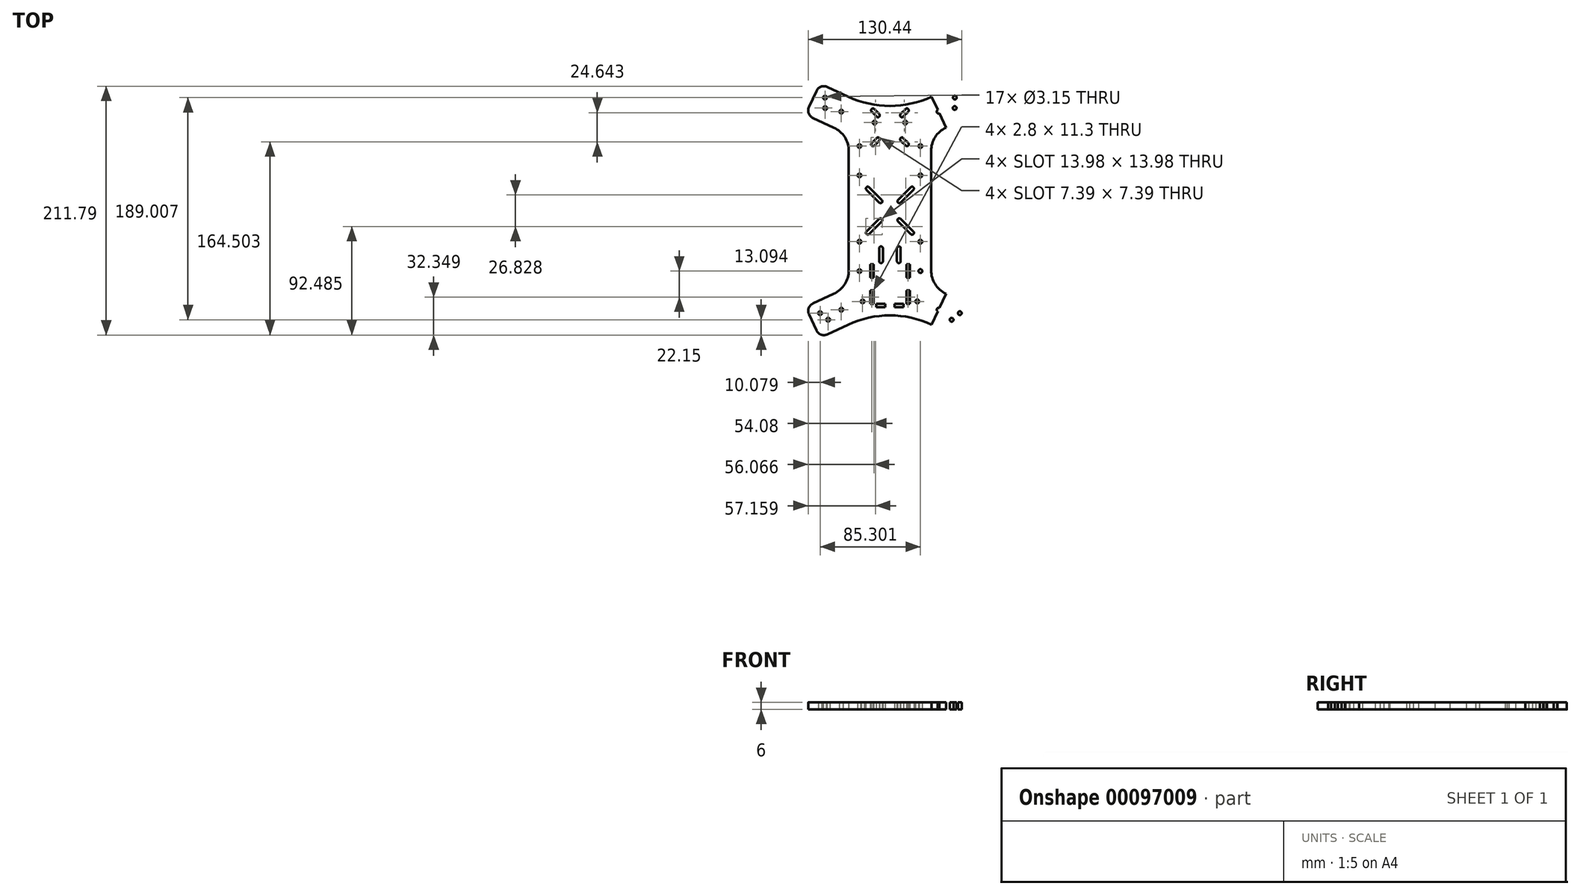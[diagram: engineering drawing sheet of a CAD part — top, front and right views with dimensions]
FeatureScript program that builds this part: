
annotation { "Feature Type Name" : "Feature", "Feature Type Description" : "" }
export const myFeature = defineFeature(function(context is Context, id is Id, definition is map)
    precondition{}
    {
        {
            var Q0;
            Q0=qCreatedBy(makeId("Top.planeOp"),FACE);
            var sketch = newSketch(context, id + "F0", { "sketchPlane" : qUnion([Q0])});
            skPoint(sketch, "E0", {"position": v(0, -1.46) * mm});
            skLineSegment(sketch, "E1", {"start": v(-16.8, -69.36) * mm, "end": v(-14, -69.36) * mm});
            skLineSegment(sketch, "E2", {"start": v(-16.8, -58.51) * mm, "end": v(-14, -58.51) * mm});
            skLineSegment(sketch, "E3", {"start": v(16.8, -47.21) * mm, "end": v(16.8, -58.51) * mm});
            skLineSegment(sketch, "E4", {"start": v(-16.8, -47.21) * mm, "end": v(-16.8, -58.51) * mm});
            skLineSegment(sketch, "E5.trimOffspring", {"start": v(-16.8, -47.21) * mm, "end": v(-14, -47.21) * mm});
            skLineSegment(sketch, "E6", {"start": v(-11.5, -80.66) * mm, "end": v(-11.5, -83.46) * mm});
            skLineSegment(sketch, "E7", {"start": v(11.5, -80.66) * mm, "end": v(11.5, -83.46) * mm});
            skLineSegment(sketch, "E8", {"start": v(4, -80.66) * mm, "end": v(4, -83.46) * mm});
            skLineSegment(sketch, "E9", {"start": v(-4, -80.66) * mm, "end": v(-4, -83.46) * mm});
            skLineSegment(sketch, "E10.trimOffspring", {"start": v(14, -69.36) * mm, "end": v(14, -80.66) * mm});
            skLineSegment(sketch, "E11.trimOffspring", {"start": v(-14, -69.36) * mm, "end": v(-14, -80.66) * mm});
            skLineSegment(sketch, "E12.trimOffspring", {"start": v(14, -69.36) * mm, "end": v(16.8, -69.36) * mm});
            skLineSegment(sketch, "E13.trimOffspring", {"start": v(14, -58.51) * mm, "end": v(16.8, -58.51) * mm});
            skLineSegment(sketch, "E14.trimOffspring", {"start": v(14, -47.21) * mm, "end": v(16.8, -47.21) * mm});
            skLineSegment(sketch, "E15.trimOffspring", {"start": v(14, -47.21) * mm, "end": v(14, -58.51) * mm});
            skLineSegment(sketch, "E16.trimOffspring", {"start": v(-14, -47.21) * mm, "end": v(-14, -58.51) * mm});
            skLineSegment(sketch, "E17", {"start": v(-16.8, -69.36) * mm, "end": v(-16.8, -80.66) * mm});
            skLineSegment(sketch, "E18", {"start": v(16.8, -69.36) * mm, "end": v(16.8, -80.66) * mm});
            skCircle(sketch, "E19", {"center": v(23.23, -78.7) * mm, "radius": 1.57 * mm});
            skCircle(sketch, "E20", {"center": v(-23.23, -78.7) * mm, "radius": 1.57 * mm});
            skCircle(sketch, "E21", {"center": v(-25.9, -52.86) * mm, "radius": 1.57 * mm});
            skCircle(sketch, "E22", {"center": v(25.9, -52.86) * mm, "radius": 1.57 * mm});
            skCircle(sketch, "E23", {"center": v(-13.04, 73.48) * mm, "radius": 1.57 * mm});
            skCircle(sketch, "E24", {"center": v(13.04, 73.48) * mm, "radius": 1.57 * mm});
            skCircle(sketch, "E25", {"center": v(-25.9, 53.54) * mm, "radius": 1.57 * mm});
            skCircle(sketch, "E26", {"center": v(25.9, 53.54) * mm, "radius": 1.57 * mm});
            skLineSegment(sketch, "E27", {"start": v(-16.8, -80.66) * mm, "end": v(-14, -80.66) * mm});
            skLineSegment(sketch, "E28", {"start": v(-11.5, -83.46) * mm, "end": v(-4, -83.46) * mm});
            skLineSegment(sketch, "E29.trimOffspring", {"start": v(4, -80.66) * mm, "end": v(11.5, -80.66) * mm});
            skLineSegment(sketch, "E30.trimOffspring", {"start": v(4, -83.46) * mm, "end": v(11.5, -83.46) * mm});
            skLineSegment(sketch, "E31.trimOffspring", {"start": v(-11.5, -80.66) * mm, "end": v(-4, -80.66) * mm});
            skLineSegment(sketch, "E32.trimOffspring", {"start": v(14, -80.66) * mm, "end": v(16.8, -80.66) * mm});
            skCircle(sketch, "E33", {"center": v(-59.4, -88.64) * mm, "radius": 1.57 * mm});
            skCircle(sketch, "E34", {"center": v(-52.49, -94.27) * mm, "radius": 1.57 * mm});
            skCircle(sketch, "E35", {"center": v(-41.34, -85.73) * mm, "radius": 1.57 * mm});
            skLineSegment(sketch, "E36", {"start": v(-57.3, -93.14) * mm, "end": v(-41.36, -85.7) * mm});
            skCircle(sketch, "E37", {"center": v(-55.2, 94.74) * mm, "radius": 1.57 * mm});
            skCircle(sketch, "E38", {"center": v(-55.06, 85.83) * mm, "radius": 1.57 * mm});
            skCircle(sketch, "E39", {"center": v(-41.34, 82.8) * mm, "radius": 1.57 * mm});
            skLineSegment(sketch, "E40", {"start": v(-57.3, 90.25) * mm, "end": v(-41.34, 82.8) * mm});
            skLineSegment(sketch, "E41.MirrorCS", {"start": v(57.29, 90.26) * mm, "end": v(41.34, 82.82) * mm});
            skCircle(sketch, "E42.MirrorC", {"center": v(55.19, 94.75) * mm, "radius": 1.57 * mm});
            skCircle(sketch, "E43.MirrorC", {"center": v(55.05, 85.84) * mm, "radius": 1.57 * mm});
            skCircle(sketch, "E44.MirrorC", {"center": v(41.34, 82.8) * mm, "radius": 1.57 * mm});
            skLineSegment(sketch, "E45.MirrorCS", {"start": v(57.3, -93.17) * mm, "end": v(41.34, -85.73) * mm});
            skCircle(sketch, "E46.MirrorC", {"center": v(59.39, -88.67) * mm, "radius": 1.57 * mm});
            skCircle(sketch, "E47.MirrorC", {"center": v(52.47, -94.3) * mm, "radius": 1.57 * mm});
            skCircle(sketch, "E48.MirrorC", {"center": v(41.34, -85.73) * mm, "radius": 1.57 * mm});
            skLineSegment(sketch, "E49", {"start": v(55.05, 85.84) * mm, "end": v(53.76, 88.61) * mm});
            skLineSegment(sketch, "E50", {"start": v(55.19, 94.75) * mm, "end": v(57.29, 90.26) * mm});
            skLineSegment(sketch, "E51", {"start": v(57.29, 90.26) * mm, "end": v(65.44, 94.06) * mm});
            skLineSegment(sketch, "E52", {"start": v(-55.06, 85.83) * mm, "end": v(-53.77, 88.6) * mm});
            skLineSegment(sketch, "E53", {"start": v(-55.2, 94.74) * mm, "end": v(-57.3, 90.25) * mm});
            skLineSegment(sketch, "E54", {"start": v(-57.3, 90.25) * mm, "end": v(-65.45, 94.05) * mm});
            skLineSegment(sketch, "E55", {"start": v(-52.49, -94.27) * mm, "end": v(-53.78, -91.5) * mm});
            skLineSegment(sketch, "E56", {"start": v(-59.4, -88.64) * mm, "end": v(-57.3, -93.14) * mm});
            skLineSegment(sketch, "E57", {"start": v(52.47, -94.3) * mm, "end": v(53.77, -91.52) * mm});
            skLineSegment(sketch, "E58", {"start": v(59.39, -88.67) * mm, "end": v(57.3, -93.17) * mm});
            skLineSegment(sketch, "E59", {"start": v(57.3, -93.17) * mm, "end": v(65.45, -96.97) * mm});
            skLineSegment(sketch, "E60", {"start": v(-57.3, -93.14) * mm, "end": v(-65.46, -96.94) * mm});
            skLineSegment(sketch, "E61", {"start": v(-65.45, 94.05) * mm, "end": v(-62.49, 100.4) * mm});
            skLineSegment(sketch, "E62", {"start": v(-65.45, 94.05) * mm, "end": v(-68.83, 86.8) * mm});
            skLineSegment(sketch, "E63", {"start": v(65.44, 94.06) * mm, "end": v(68.79, 86.89) * mm});
            skLineSegment(sketch, "E64", {"start": v(65.44, 94.06) * mm, "end": v(62.49, 100.4) * mm});
            skLineSegment(sketch, "E65", {"start": v(65.45, -96.97) * mm, "end": v(68.83, -89.72) * mm});
            skLineSegment(sketch, "E66", {"start": v(65.45, -96.97) * mm, "end": v(62.49, -103.31) * mm});
            skLineSegment(sketch, "E67", {"start": v(-65.46, -96.94) * mm, "end": v(-68.83, -89.72) * mm});
            skLineSegment(sketch, "E68", {"start": v(-65.46, -96.94) * mm, "end": v(-62.5, -103.3) * mm});
            skLineSegment(sketch, "E69", {"start": v(-13.04, 73.48) * mm, "end": v(-13.04, 71.9) * mm});
            skLineSegment(sketch, "E70", {"start": v(13.04, 73.48) * mm, "end": v(13.04, 71.9) * mm});
            skLineSegment(sketch, "E71", {"start": v(13.04, 71.9) * mm, "end": v(-13.04, 71.9) * mm});
            skLineSegment(sketch, "E72", {"start": v(-4, -83.46) * mm, "end": v(4, -83.46) * mm});
            skLineSegment(sketch, "E73", {"start": v(0, -1.46) * mm, "end": v(0, 14.54) * mm});
            skLineSegment(sketch, "E74", {"start": v(0, -1.46) * mm, "end": v(0, -17.46) * mm});
            skLineSegment(sketch, "E75", {"start": v(-25.9, 53.54) * mm, "end": v(-25.9, 51.96) * mm});
            skLineSegment(sketch, "E76", {"start": v(25.9, 51.96) * mm, "end": v(25.9, 53.54) * mm});
            skLineSegment(sketch, "E77", {"start": v(0, -1.46) * mm, "end": v(-16, -1.46) * mm});
            skLineSegment(sketch, "E78", {"start": v(0, -1.46) * mm, "end": v(16, -1.46) * mm});
            skLineSegment(sketch, "E79", {"start": v(-41.34, -85.73) * mm, "end": v(-35.43, -98.42) * mm});
            skLineSegment(sketch, "E80", {"start": v(-41.34, -85.73) * mm, "end": v(-47.68, -72.14) * mm});
            skLineSegment(sketch, "E81", {"start": v(-35.43, -98.42) * mm, "end": v(-53.19, -106.7) * mm});
            skLineSegment(sketch, "E82", {"start": v(-47.68, -72.14) * mm, "end": v(-65.44, -80.42) * mm});
            skLineSegment(sketch, "E83", {"start": v(41.34, -85.73) * mm, "end": v(35.43, -98.42) * mm});
            skLineSegment(sketch, "E84", {"start": v(41.34, -85.73) * mm, "end": v(47.68, -72.14) * mm});
            skLineSegment(sketch, "E85", {"start": v(47.68, -72.14) * mm, "end": v(65.44, -80.42) * mm});
            skLineSegment(sketch, "E86", {"start": v(35.43, -98.42) * mm, "end": v(53.19, -106.7) * mm});
            skLineSegment(sketch, "E87", {"start": v(-41.34, 82.8) * mm, "end": v(-35.43, 95.5) * mm});
            skLineSegment(sketch, "E88", {"start": v(-41.34, 82.8) * mm, "end": v(-47.68, 69.21) * mm});
            skLineSegment(sketch, "E89", {"start": v(41.34, 82.8) * mm, "end": v(35.43, 95.5) * mm});
            skLineSegment(sketch, "E90", {"start": v(41.34, 82.8) * mm, "end": v(47.68, 69.21) * mm});
            skLineSegment(sketch, "E91", {"start": v(35.43, 95.5) * mm, "end": v(53.19, 103.78) * mm});
            skLineSegment(sketch, "E92", {"start": v(47.68, 69.21) * mm, "end": v(65.44, 77.5) * mm});
            skLineSegment(sketch, "E93", {"start": v(-35.43, 95.5) * mm, "end": v(-53.19, 103.78) * mm});
            skLineSegment(sketch, "E94", {"start": v(-47.68, 69.21) * mm, "end": v(-65.44, 77.5) * mm});
            skLineSegment(sketch, "E95", {"start": v(-41.34, -85.73) * mm, "end": v(-35, -82.77) * mm});
            skLineSegment(sketch, "E96", {"start": v(41.34, -85.73) * mm, "end": v(35, -82.77) * mm});
            skLineSegment(sketch, "E97", {"start": v(-41.34, 82.8) * mm, "end": v(-35, 79.85) * mm});
            skLineSegment(sketch, "E98", {"start": v(41.34, 82.8) * mm, "end": v(35, 79.85) * mm});
            skLineSegment(sketch, "E99", {"start": v(16, -1.46) * mm, "end": v(35, -1.46) * mm});
            skLineSegment(sketch, "E100", {"start": v(-16, -1.46) * mm, "end": v(-35, -1.46) * mm});
            skLineSegment(sketch, "E101", {"start": v(35, -1.46) * mm, "end": v(35, 38.54) * mm});
            skLineSegment(sketch, "E102", {"start": v(35, -1.46) * mm, "end": v(35, -41.46) * mm});
            skLineSegment(sketch, "E103", {"start": v(-35, -1.46) * mm, "end": v(-35, 38.54) * mm});
            skLineSegment(sketch, "E104", {"start": v(-35, -1.46) * mm, "end": v(-35, -41.46) * mm});
            skLineSegment(sketch, "E105", {"start": v(-35, -41.46) * mm, "end": v(35, -41.46) * mm});
            skLineSegment(sketch, "E106", {"start": v(-35, 38.54) * mm, "end": v(35, 38.54) * mm});
            skLineSegment(sketch, "E107", {"start": v(-25.9, -52.86) * mm, "end": v(-25.9, -54.44) * mm});
            skLineSegment(sketch, "E108", {"start": v(-25.9, -54.44) * mm, "end": v(25.9, -54.44) * mm});
            skLineSegment(sketch, "E109", {"start": v(25.9, -54.44) * mm, "end": v(25.9, -52.86) * mm});
            skLineSegment(sketch, "E110", {"start": v(-23.23, -78.7) * mm, "end": v(-23.23, -80.27) * mm});
            skLineSegment(sketch, "E111", {"start": v(-23.23, -80.27) * mm, "end": v(23.23, -80.27) * mm});
            skLineSegment(sketch, "E112", {"start": v(23.23, -80.27) * mm, "end": v(23.23, -78.7) * mm});
            skLineSegment(sketch, "E113", {"start": v(35, 79.85) * mm, "end": v(35, 38.54) * mm});
            skLineSegment(sketch, "E114", {"start": v(35, -41.46) * mm, "end": v(35, -82.77) * mm});
            skLineSegment(sketch, "E115", {"start": v(-35, -82.77) * mm, "end": v(-35, -41.46) * mm});
            skLineSegment(sketch, "E116", {"start": v(-35, 38.54) * mm, "end": v(-35, 79.85) * mm});
            skLineSegment(sketch, "E117", {"start": v(-13.77, 14.54) * mm, "end": v(0, 14.54) * mm});
            skLineSegment(sketch, "E118", {"start": v(0, 14.54) * mm, "end": v(13.77, 14.54) * mm});
            skLineSegment(sketch, "E119", {"start": v(16, 12.31) * mm, "end": v(16, -1.46) * mm});
            skLineSegment(sketch, "E120", {"start": v(16, -1.46) * mm, "end": v(16, -15.23) * mm});
            skLineSegment(sketch, "E121", {"start": v(13.77, -17.46) * mm, "end": v(0, -17.46) * mm});
            skLineSegment(sketch, "E122", {"start": v(0, -17.46) * mm, "end": v(-13.77, -17.46) * mm});
            skLineSegment(sketch, "E123", {"start": v(-16, -15.23) * mm, "end": v(-16, -1.46) * mm});
            skLineSegment(sketch, "E124", {"start": v(-16, -1.46) * mm, "end": v(-16, 12.31) * mm});
            skPoint(sketch, "E125", {"position": v(-35, 49.3) * mm});
            skPoint(sketch, "E126", {"position": v(35, 49.3) * mm});
            skPoint(sketch, "E127", {"position": v(-35, -52.23) * mm});
            skPoint(sketch, "E128", {"position": v(35, -52.23) * mm});
            skLineSegment(sketch, "E129", {"start": v(0, -54.44) * mm, "end": v(0, -80.27) * mm});
            skLineSegment(sketch, "E130", {"start": v(0, -80.27) * mm, "end": v(0, -83.46) * mm});
            skLineSegment(sketch, "E131", {"start": v(47.68, 69.21) * mm, "end": v(35, 63.3) * mm});
            skLineSegment(sketch, "E132", {"start": v(-47.68, 69.21) * mm, "end": v(-35, 63.3) * mm});
            skLineSegment(sketch, "E133", {"start": v(47.68, -72.14) * mm, "end": v(35, -66.22) * mm});
            skLineSegment(sketch, "E134", {"start": v(-47.68, -72.14) * mm, "end": v(-35, -66.22) * mm});
            skArc(sketch, "E135", {"start": v(-47.68, 69.21) * mm, "mid": v(-38.44, 61.1) * mm, "end": v(-35, 49.3) * mm});
            skArc(sketch, "E136", {"start": v(47.68, 69.21) * mm, "mid": v(38.44, 61.1) * mm, "end": v(35, 49.3) * mm});
            skArc(sketch, "E137", {"start": v(47.68, -72.14) * mm, "mid": v(38.44, -64.03) * mm, "end": v(35, -52.23) * mm});
            skArc(sketch, "E138", {"start": v(-47.68, -72.14) * mm, "mid": v(-38.44, -64.03) * mm, "end": v(-35, -52.23) * mm});
            skArc(sketch, "E139", {"start": v(35.43, 95.5) * mm, "mid": v(0, 87.64) * mm, "end": v(-35.43, 95.5) * mm});
            skArc(sketch, "E140", {"start": v(35.43, -98.42) * mm, "mid": v(0, -90.57) * mm, "end": v(-35.43, -98.42) * mm});
            skLineSegment(sketch, "E141", {"start": v(0, -83.46) * mm, "end": v(0, -90.57) * mm});
            skLineSegment(sketch, "E142", {"start": v(0, 71.9) * mm, "end": v(0, 87.64) * mm});
            skLineSegment(sketch, "E143", {"start": v(0, 71.9) * mm, "end": v(0, 51.96) * mm});
            skLineSegment(sketch, "E144", {"start": v(-25.9, 51.96) * mm, "end": v(25.9, 51.96) * mm});
            skLineSegment(sketch, "E145", {"start": v(-25.9, -52.86) * mm, "end": v(-25.9, 53.54) * mm});
            skLineSegment(sketch, "E146", {"start": v(25.9, 53.54) * mm, "end": v(25.9, -52.86) * mm});
            skPoint(sketch, "E147", {"position": v(25.9, -27.86) * mm});
            skPoint(sketch, "E148", {"position": v(-25.9, -27.86) * mm});
            skPoint(sketch, "E149", {"position": v(-25.9, 28.54) * mm});
            skPoint(sketch, "E150", {"position": v(25.9, 28.54) * mm});
            skCircle(sketch, "E151", {"center": v(25.9, 28.54) * mm, "radius": 1.57 * mm});
            skCircle(sketch, "E152", {"center": v(-25.9, 28.54) * mm, "radius": 1.57 * mm});
            skCircle(sketch, "E153", {"center": v(-25.9, -27.86) * mm, "radius": 1.57 * mm});
            skCircle(sketch, "E154", {"center": v(25.9, -27.86) * mm, "radius": 1.57 * mm});
            skPoint(sketch, "E155", {"position": v(0, -41.46) * mm});
            skPoint(sketch, "E156", {"position": v(-6, -41.46) * mm});
            skPoint(sketch, "E157", {"position": v(6, -41.46) * mm});
            skPoint(sketch, "E158", {"position": v(9.15, -41.46) * mm});
            skPoint(sketch, "E159", {"position": v(-9.15, -41.46) * mm});
            skLineSegment(sketch, "E160", {"start": v(-9.15, -41.46) * mm, "end": v(-9.15, -33.46) * mm});
            skLineSegment(sketch, "E161", {"start": v(-6, -41.46) * mm, "end": v(-6, -33.46) * mm});
            skLineSegment(sketch, "E162", {"start": v(6, -41.46) * mm, "end": v(6, -33.46) * mm});
            skLineSegment(sketch, "E163", {"start": v(9.15, -41.46) * mm, "end": v(9.15, -33.46) * mm});
            skLineSegment(sketch, "E164", {"start": v(-9.15, -41.46) * mm, "end": v(-9.15, -44.46) * mm});
            skLineSegment(sketch, "E165", {"start": v(-6, -41.46) * mm, "end": v(-6, -44.46) * mm});
            skLineSegment(sketch, "E166", {"start": v(6, -41.46) * mm, "end": v(6, -44.46) * mm});
            skLineSegment(sketch, "E167", {"start": v(9.15, -41.46) * mm, "end": v(9.15, -44.46) * mm});
            skArc(sketch, "E168", {"start": v(-6, -33.46) * mm, "mid": v(-7.58, -31.89) * mm, "end": v(-9.15, -33.46) * mm});
            skArc(sketch, "E169", {"start": v(-9.15, -44.46) * mm, "mid": v(-7.58, -46.04) * mm, "end": v(-6, -44.46) * mm});
            skArc(sketch, "E170", {"start": v(6, -44.46) * mm, "mid": v(7.57, -46.04) * mm, "end": v(9.15, -44.46) * mm});
            skArc(sketch, "E171", {"start": v(9.15, -33.46) * mm, "mid": v(7.57, -31.89) * mm, "end": v(6, -33.46) * mm});
            skLineSegment(sketch, "E172", {"start": v(0, -1.46) * mm, "end": v(6.89, 5.43) * mm});
            skLineSegment(sketch, "E173", {"start": v(0, -1.46) * mm, "end": v(-6.89, 5.43) * mm});
            skLineSegment(sketch, "E174", {"start": v(0, -1.46) * mm, "end": v(6.89, -8.35) * mm});
            skLineSegment(sketch, "E175", {"start": v(0, -1.46) * mm, "end": v(-6.89, -8.35) * mm});
            skArc(sketch, "E176", {"start": v(17.71, -21.4) * mm, "mid": v(19.94, -21.4) * mm, "end": v(19.94, -19.18) * mm});
            skArc(sketch, "E177", {"start": v(-19.94, -19.18) * mm, "mid": v(-19.94, -21.4) * mm, "end": v(-17.71, -21.4) * mm});
            skArc(sketch, "E178", {"start": v(-17.71, 18.48) * mm, "mid": v(-19.94, 18.48) * mm, "end": v(-19.94, 16.25) * mm});
            skArc(sketch, "E179", {"start": v(19.94, 16.25) * mm, "mid": v(19.94, 18.48) * mm, "end": v(17.71, 18.48) * mm});
            skPoint(sketch, "E180", {"position": v(8, 6.54) * mm});
            skPoint(sketch, "E181", {"position": v(-8, 6.54) * mm});
            skPoint(sketch, "E182", {"position": v(8, -9.46) * mm});
            skPoint(sketch, "E183", {"position": v(-8, -9.46) * mm});
            skArc(sketch, "E184", {"start": v(6.89, 7.65) * mm, "mid": v(6.89, 5.43) * mm, "end": v(9.11, 5.43) * mm});
            skArc(sketch, "E185", {"start": v(-9.11, 5.43) * mm, "mid": v(-6.89, 5.43) * mm, "end": v(-6.89, 7.65) * mm});
            skArc(sketch, "E186", {"start": v(9.11, -8.35) * mm, "mid": v(6.89, -8.35) * mm, "end": v(6.89, -10.57) * mm});
            skArc(sketch, "E187", {"start": v(-6.89, -10.57) * mm, "mid": v(-6.89, -8.35) * mm, "end": v(-9.11, -8.35) * mm});
            skLineSegment(sketch, "E188", {"start": v(17.71, 18.48) * mm, "end": v(6.89, 7.65) * mm});
            skLineSegment(sketch, "E189", {"start": v(9.11, 5.43) * mm, "end": v(19.94, 16.25) * mm});
            skLineSegment(sketch, "E190", {"start": v(-6.89, 7.65) * mm, "end": v(-17.71, 18.48) * mm});
            skLineSegment(sketch, "E191", {"start": v(-19.94, 16.25) * mm, "end": v(-9.11, 5.43) * mm});
            skLineSegment(sketch, "E192", {"start": v(17.71, -21.4) * mm, "end": v(6.89, -10.57) * mm});
            skLineSegment(sketch, "E193", {"start": v(9.11, -8.35) * mm, "end": v(19.94, -19.18) * mm});
            skLineSegment(sketch, "E194", {"start": v(-6.89, -10.57) * mm, "end": v(-17.71, -21.4) * mm});
            skLineSegment(sketch, "E195", {"start": v(-19.94, -19.18) * mm, "end": v(-9.11, -8.35) * mm});
            skPoint(sketch, "E196", {"position": v(-19.94, -21.4) * mm});
            skPoint(sketch, "E197", {"position": v(62.49, -103.31) * mm});
            skPoint(sketch, "E198", {"position": v(68.83, -89.72) * mm});
            skPoint(sketch, "E199", {"position": v(65.44, -80.42) * mm});
            skPoint(sketch, "E200", {"position": v(53.19, -106.7) * mm});
            skArc(sketch, "E201", {"start": v(53.19, -106.7) * mm, "mid": v(58.54, -106.93) * mm, "end": v(62.49, -103.31) * mm});
            skArc(sketch, "E202", {"start": v(65.44, -80.42) * mm, "mid": v(69.06, -84.37) * mm, "end": v(68.83, -89.72) * mm});
            skPoint(sketch, "E203", {"position": v(-53.19, -106.7) * mm});
            skPoint(sketch, "E204", {"position": v(-62.5, -103.3) * mm});
            skArc(sketch, "E205", {"start": v(-53.19, -106.7) * mm, "mid": v(-58.55, -106.93) * mm, "end": v(-62.5, -103.3) * mm});
            skPoint(sketch, "E206", {"position": v(-68.83, -89.72) * mm});
            skPoint(sketch, "E207", {"position": v(-65.44, -80.42) * mm});
            skArc(sketch, "E208", {"start": v(-65.44, -80.42) * mm, "mid": v(-69.06, -84.37) * mm, "end": v(-68.83, -89.72) * mm});
            skPoint(sketch, "E209", {"position": v(-65.44, 77.5) * mm});
            skPoint(sketch, "E210", {"position": v(-68.83, 86.8) * mm});
            skPoint(sketch, "E211", {"position": v(-62.49, 100.4) * mm});
            skPoint(sketch, "E212", {"position": v(-53.19, 103.78) * mm});
            skArc(sketch, "E213", {"start": v(-65.44, 77.5) * mm, "mid": v(-69.06, 81.45) * mm, "end": v(-68.83, 86.8) * mm});
            skArc(sketch, "E214", {"start": v(-53.19, 103.78) * mm, "mid": v(-58.54, 104.01) * mm, "end": v(-62.49, 100.4) * mm});
            skPoint(sketch, "E215", {"position": v(53.19, 103.78) * mm});
            skPoint(sketch, "E216", {"position": v(62.49, 100.4) * mm});
            skPoint(sketch, "E217", {"position": v(68.79, 86.89) * mm});
            skPoint(sketch, "E218", {"position": v(65.44, 77.5) * mm});
            skArc(sketch, "E219", {"start": v(65.44, 77.5) * mm, "mid": v(69.08, 81.5) * mm, "end": v(68.79, 86.89) * mm});
            skArc(sketch, "E220", {"start": v(53.19, 103.78) * mm, "mid": v(58.54, 104.01) * mm, "end": v(62.49, 100.4) * mm});
            skLineSegment(sketch, "E221", {"start": v(0, 69.46) * mm, "end": v(-9.09, 78.55) * mm});
            skLineSegment(sketch, "E222", {"start": v(0, 69.46) * mm, "end": v(9.09, 78.55) * mm});
            skLineSegment(sketch, "E223", {"start": v(0, 69.46) * mm, "end": v(9.09, 60.38) * mm});
            skLineSegment(sketch, "E224", {"start": v(0, 69.46) * mm, "end": v(-9.09, 60.38) * mm});
            skArc(sketch, "E225", {"start": v(15.56, 82.8) * mm, "mid": v(15.56, 85.02) * mm, "end": v(13.33, 85.02) * mm});
            skArc(sketch, "E226", {"start": v(13.33, 53.9) * mm, "mid": v(15.56, 53.9) * mm, "end": v(15.56, 56.14) * mm});
            skArc(sketch, "E227", {"start": v(-15.56, 56.14) * mm, "mid": v(-15.56, 53.9) * mm, "end": v(-13.33, 53.9) * mm});
            skArc(sketch, "E228", {"start": v(-13.33, 85.02) * mm, "mid": v(-15.56, 85.02) * mm, "end": v(-15.56, 82.8) * mm});
            skArc(sketch, "E229", {"start": v(9.09, 80.78) * mm, "mid": v(9.09, 78.55) * mm, "end": v(11.31, 78.55) * mm});
            skLineSegment(sketch, "E230", {"start": v(11.31, 78.55) * mm, "end": v(15.56, 82.8) * mm});
            skLineSegment(sketch, "E231", {"start": v(13.33, 85.02) * mm, "end": v(9.09, 80.78) * mm});
            skArc(sketch, "E232", {"start": v(-11.31, 78.55) * mm, "mid": v(-9.09, 78.55) * mm, "end": v(-9.09, 80.78) * mm});
            skLineSegment(sketch, "E233", {"start": v(-11.31, 78.55) * mm, "end": v(-15.56, 82.8) * mm});
            skLineSegment(sketch, "E234", {"start": v(-9.09, 80.78) * mm, "end": v(-13.33, 85.02) * mm});
            skArc(sketch, "E235", {"start": v(11.31, 60.38) * mm, "mid": v(9.09, 60.38) * mm, "end": v(9.09, 58.15) * mm});
            skLineSegment(sketch, "E236", {"start": v(9.09, 58.15) * mm, "end": v(13.33, 53.9) * mm});
            skLineSegment(sketch, "E237", {"start": v(11.31, 60.38) * mm, "end": v(15.56, 56.14) * mm});
            skArc(sketch, "E238", {"start": v(-9.09, 58.15) * mm, "mid": v(-9.09, 60.38) * mm, "end": v(-11.31, 60.38) * mm});
            skLineSegment(sketch, "E239", {"start": v(-9.09, 58.15) * mm, "end": v(-13.33, 53.9) * mm});
            skLineSegment(sketch, "E240", {"start": v(-11.31, 60.38) * mm, "end": v(-15.56, 56.14) * mm});
            skSolve(sketch);
        }
        {
            var Q0;
            Q0=makeQuery(id+"F0.imprint","IMPRINT",FACE,{"disambiguationData":[TD([[makeQuery(id+"F0.imprint","IMPRINT",EDGE,{"derivedFrom":sQuery(id+"F0.wireOp",EDGE,"E37")}),-1.0]])]});
            var Q1;
            Q1=makeQuery(id+"F0.imprint","IMPRINT",FACE,{"disambiguationData":[TD([[makeQuery(id+"F0.imprint","IMPRINT",EDGE,{"derivedFrom":sQuery(id+"F0.wireOp",EDGE,"E38")}),-1.0]])]});
            var Q2;
            {var subQ3=sQuery(id+"F0.wireOp",EDGE,"E132");Q2=makeQuery(id+"F0.imprint","IMPRINT",FACE,{"disambiguationData":[TD([[makeQuery(id+"F0.imprint","IMPRINT",EDGE,{"derivedFrom":subQ3}),1.0]])]});}
            var Q3;
            Q3=makeQuery(id+"F0.imprint","IMPRINT",FACE,{"disambiguationData":[TD([[makeQuery(id+"F0.imprint","IMPRINT",EDGE,{"derivedFrom":sQuery(id+"F0.wireOp",EDGE,"E23")}),-1.0]])]});
            var Q4;
            Q4=makeQuery(id+"F0.imprint","IMPRINT",FACE,{"disambiguationData":[TD([[makeQuery(id+"F0.imprint","IMPRINT",EDGE,{"derivedFrom":sQuery(id+"F0.wireOp",EDGE,"E24")}),-1.0]])]});
            var Q5;
            Q5=makeQuery(id+"F0.imprint","IMPRINT",FACE,{"disambiguationData":[TD([[makeQuery(id+"F0.imprint","IMPRINT",EDGE,{"derivedFrom":sQuery(id+"F0.wireOp",EDGE,"E42.MirrorC")}),1.0]])]});
            var Q6;
            Q6=makeQuery(id+"F0.imprint","IMPRINT",FACE,{"disambiguationData":[TD([[makeQuery(id+"F0.imprint","IMPRINT",EDGE,{"derivedFrom":sQuery(id+"F0.wireOp",EDGE,"E43.MirrorC")}),1.0]])]});
            var Q7;
            {var subQ3=sQuery(id+"F0.wireOp",EDGE,"E131");Q7=makeQuery(id+"F0.imprint","IMPRINT",FACE,{"disambiguationData":[TD([[makeQuery(id+"F0.imprint","IMPRINT",EDGE,{"derivedFrom":subQ3}),-1.0]])]});}
            var Q8;
            {var subQ0=sQuery(id+"F0.wireOp",EDGE,"E132");Q8=makeQuery(id+"F0.imprint","IMPRINT",FACE,{"disambiguationData":[TD([[makeQuery(id+"F0.imprint","IMPRINT",EDGE,{"derivedFrom":subQ0}),-1.0]])]});}
            var Q9;
            {var subQ0=sQuery(id+"F0.wireOp",EDGE,"E131");Q9=makeQuery(id+"F0.imprint","IMPRINT",FACE,{"disambiguationData":[TD([[makeQuery(id+"F0.imprint","IMPRINT",EDGE,{"derivedFrom":subQ0}),1.0]])]});}
            var Q10;
            {var subQ1=sQuery(id+"F0.wireOp",EDGE,"E71");var subQ3=sQuery(id+"F0.wireOp",EDGE,"E221");var subQ4=makeQuery(id+"F0.imprint","INTERSECT",VERTEX,{"derivedFrom":[subQ1,subQ3]});Q10=makeQuery(id+"F0.imprint","IMPRINT",FACE,{"disambiguationData":[TD([[makeQuery(id+"F0.imprint","IMPRINT",EDGE,{"disambiguationData":[TD([[subQ4,1.0]])],"derivedFrom":subQ1}),1.0]])]});}
            var Q11;
            {var subQ1=sQuery(id+"F0.wireOp",EDGE,"E71");var subQ3=sQuery(id+"F0.wireOp",EDGE,"E222");var subQ4=makeQuery(id+"F0.imprint","INTERSECT",VERTEX,{"derivedFrom":[subQ1,subQ3]});Q11=makeQuery(id+"F0.imprint","IMPRINT",FACE,{"disambiguationData":[TD([[makeQuery(id+"F0.imprint","IMPRINT",EDGE,{"disambiguationData":[TD([[subQ4,-1.0]])],"derivedFrom":subQ1}),1.0]])]});}
            var Q12;
            {var subQ0=sQuery(id+"F0.wireOp",EDGE,"E145");var subQ3=sQuery(id+"F0.wireOp",EDGE,"E106");var subQ4=makeQuery(id+"F0.imprint","INTERSECT",VERTEX,{"derivedFrom":[subQ3,subQ0]});Q12=makeQuery(id+"F0.imprint","IMPRINT",FACE,{"disambiguationData":[TD([[makeQuery(id+"F0.imprint","IMPRINT",EDGE,{"disambiguationData":[TD([[subQ4,-1.0]])],"derivedFrom":subQ3}),1.0]])]});}
            var Q13;
            {var subQ18=sQuery(id+"F0.wireOp",EDGE,"E117");Q13=makeQuery(id+"F0.imprint","IMPRINT",FACE,{"disambiguationData":[TD([[makeQuery(id+"F0.imprint","IMPRINT",EDGE,{"derivedFrom":subQ18}),1.0]])]});}
            var Q14;
            {var subQ6=sQuery(id+"F0.wireOp",EDGE,"E103");Q14=makeQuery(id+"F0.imprint","IMPRINT",FACE,{"disambiguationData":[TD([[makeQuery(id+"F0.imprint","IMPRINT",EDGE,{"derivedFrom":subQ6}),-1.0]])]});}
            var Q15;
            {var subQ5=sQuery(id+"F0.wireOp",EDGE,"E101");Q15=makeQuery(id+"F0.imprint","IMPRINT",FACE,{"disambiguationData":[TD([[makeQuery(id+"F0.imprint","IMPRINT",EDGE,{"derivedFrom":subQ5}),1.0]])]});}
            var Q16;
            Q16=makeQuery(id+"F0.imprint","IMPRINT",FACE,{"disambiguationData":[TD([[makeQuery(id+"F0.imprint","IMPRINT",EDGE,{"derivedFrom":sQuery(id+"F0.wireOp",EDGE,"E73")}),-1.0]])]});
            var Q17;
            Q17=makeQuery(id+"F0.imprint","IMPRINT",FACE,{"disambiguationData":[TD([[makeQuery(id+"F0.imprint","IMPRINT",EDGE,{"derivedFrom":sQuery(id+"F0.wireOp",EDGE,"E73")}),1.0]])]});
            var Q18;
            Q18=makeQuery(id+"F0.imprint","IMPRINT",FACE,{"disambiguationData":[TD([[makeQuery(id+"F0.imprint","IMPRINT",EDGE,{"derivedFrom":sQuery(id+"F0.wireOp",EDGE,"E77")}),-1.0]])]});
            var Q19;
            Q19=makeQuery(id+"F0.imprint","IMPRINT",FACE,{"disambiguationData":[TD([[makeQuery(id+"F0.imprint","IMPRINT",EDGE,{"derivedFrom":sQuery(id+"F0.wireOp",EDGE,"E78")}),1.0]])]});
            var Q20;
            Q20=makeQuery(id+"F0.imprint","IMPRINT",FACE,{"disambiguationData":[TD([[makeQuery(id+"F0.imprint","IMPRINT",EDGE,{"derivedFrom":sQuery(id+"F0.wireOp",EDGE,"E78")}),-1.0]])]});
            var Q21;
            Q21=makeQuery(id+"F0.imprint","IMPRINT",FACE,{"disambiguationData":[TD([[makeQuery(id+"F0.imprint","IMPRINT",EDGE,{"derivedFrom":sQuery(id+"F0.wireOp",EDGE,"E74")}),1.0]])]});
            var Q22;
            Q22=makeQuery(id+"F0.imprint","IMPRINT",FACE,{"disambiguationData":[TD([[makeQuery(id+"F0.imprint","IMPRINT",EDGE,{"derivedFrom":sQuery(id+"F0.wireOp",EDGE,"E74")}),-1.0]])]});
            var Q23;
            Q23=makeQuery(id+"F0.imprint","IMPRINT",FACE,{"disambiguationData":[TD([[makeQuery(id+"F0.imprint","IMPRINT",EDGE,{"derivedFrom":sQuery(id+"F0.wireOp",EDGE,"E77")}),1.0]])]});
            var Q24;
            {var subQ5=sQuery(id+"F0.wireOp",EDGE,"E104");Q24=makeQuery(id+"F0.imprint","IMPRINT",FACE,{"disambiguationData":[TD([[makeQuery(id+"F0.imprint","IMPRINT",EDGE,{"derivedFrom":subQ5}),1.0]])]});}
            var Q25;
            {var subQ20=sQuery(id+"F0.wireOp",EDGE,"E120");Q25=makeQuery(id+"F0.imprint","IMPRINT",FACE,{"disambiguationData":[TD([[makeQuery(id+"F0.imprint","IMPRINT",EDGE,{"derivedFrom":subQ20}),1.0]])]});}
            var Q26;
            {var subQ5=sQuery(id+"F0.wireOp",EDGE,"E102");Q26=makeQuery(id+"F0.imprint","IMPRINT",FACE,{"disambiguationData":[TD([[makeQuery(id+"F0.imprint","IMPRINT",EDGE,{"derivedFrom":subQ5}),-1.0]])]});}
            var Q27;
            {var subQ25=sQuery(id+"F0.wireOp",EDGE,"E1");Q27=makeQuery(id+"F0.imprint","IMPRINT",FACE,{"disambiguationData":[TD([[makeQuery(id+"F0.imprint","IMPRINT",EDGE,{"derivedFrom":subQ25}),1.0]])]});}
            var Q28;
            {var subQ25=sQuery(id+"F0.wireOp",EDGE,"E5.trimOffspring");Q28=makeQuery(id+"F0.imprint","IMPRINT",FACE,{"disambiguationData":[TD([[makeQuery(id+"F0.imprint","IMPRINT",EDGE,{"derivedFrom":subQ25}),1.0]])]});}
            var Q29;
            Q29=makeQuery(id+"F0.imprint","IMPRINT",FACE,{"disambiguationData":[TD([[makeQuery(id+"F0.imprint","IMPRINT",EDGE,{"derivedFrom":sQuery(id+"F0.wireOp",EDGE,"E7")}),1.0]])]});
            var Q30;
            {var subQ0=sQuery(id+"F0.wireOp",EDGE,"E133");Q30=makeQuery(id+"F0.imprint","IMPRINT",FACE,{"disambiguationData":[TD([[makeQuery(id+"F0.imprint","IMPRINT",EDGE,{"derivedFrom":subQ0}),-1.0]])]});}
            var Q31;
            {var subQ0=sQuery(id+"F0.wireOp",EDGE,"E134");Q31=makeQuery(id+"F0.imprint","IMPRINT",FACE,{"disambiguationData":[TD([[makeQuery(id+"F0.imprint","IMPRINT",EDGE,{"derivedFrom":subQ0}),1.0]])]});}
            var Q32;
            {var subQ5=sQuery(id+"F0.wireOp",EDGE,"E134");Q32=makeQuery(id+"F0.imprint","IMPRINT",FACE,{"disambiguationData":[TD([[makeQuery(id+"F0.imprint","IMPRINT",EDGE,{"derivedFrom":subQ5}),-1.0]])]});}
            var Q33;
            Q33=makeQuery(id+"F0.imprint","IMPRINT",FACE,{"disambiguationData":[TD([[makeQuery(id+"F0.imprint","IMPRINT",EDGE,{"derivedFrom":sQuery(id+"F0.wireOp",EDGE,"E33")}),-1.0]])]});
            var Q34;
            Q34=makeQuery(id+"F0.imprint","IMPRINT",FACE,{"disambiguationData":[TD([[makeQuery(id+"F0.imprint","IMPRINT",EDGE,{"derivedFrom":sQuery(id+"F0.wireOp",EDGE,"E34")}),-1.0]])]});
            var Q35;
            {var subQ3=sQuery(id+"F0.wireOp",EDGE,"E133");Q35=makeQuery(id+"F0.imprint","IMPRINT",FACE,{"disambiguationData":[TD([[makeQuery(id+"F0.imprint","IMPRINT",EDGE,{"derivedFrom":subQ3}),1.0]])]});}
            var Q36;
            Q36=makeQuery(id+"F0.imprint","IMPRINT",FACE,{"disambiguationData":[TD([[makeQuery(id+"F0.imprint","IMPRINT",EDGE,{"derivedFrom":sQuery(id+"F0.wireOp",EDGE,"E46.MirrorC")}),1.0]])]});
            var Q37;
            Q37=makeQuery(id+"F0.imprint","IMPRINT",FACE,{"disambiguationData":[TD([[makeQuery(id+"F0.imprint","IMPRINT",EDGE,{"derivedFrom":sQuery(id+"F0.wireOp",EDGE,"E47.MirrorC")}),1.0]])]});
            extrude(context, id + "F1", {"entities" : qUnion([Q0, Q1, Q2, Q3, Q4, Q5, Q6, Q7, Q8, Q9, Q10, Q11, Q12, Q13, Q14, Q15, Q16, Q17, Q18, Q19, Q20, Q21, Q22, Q23, Q24, Q25, Q26, Q27, Q28, Q29, Q30, Q31, Q32, Q33, Q34, Q35, Q36, Q37]), "depth" : 6 * mm});
        }
    });
